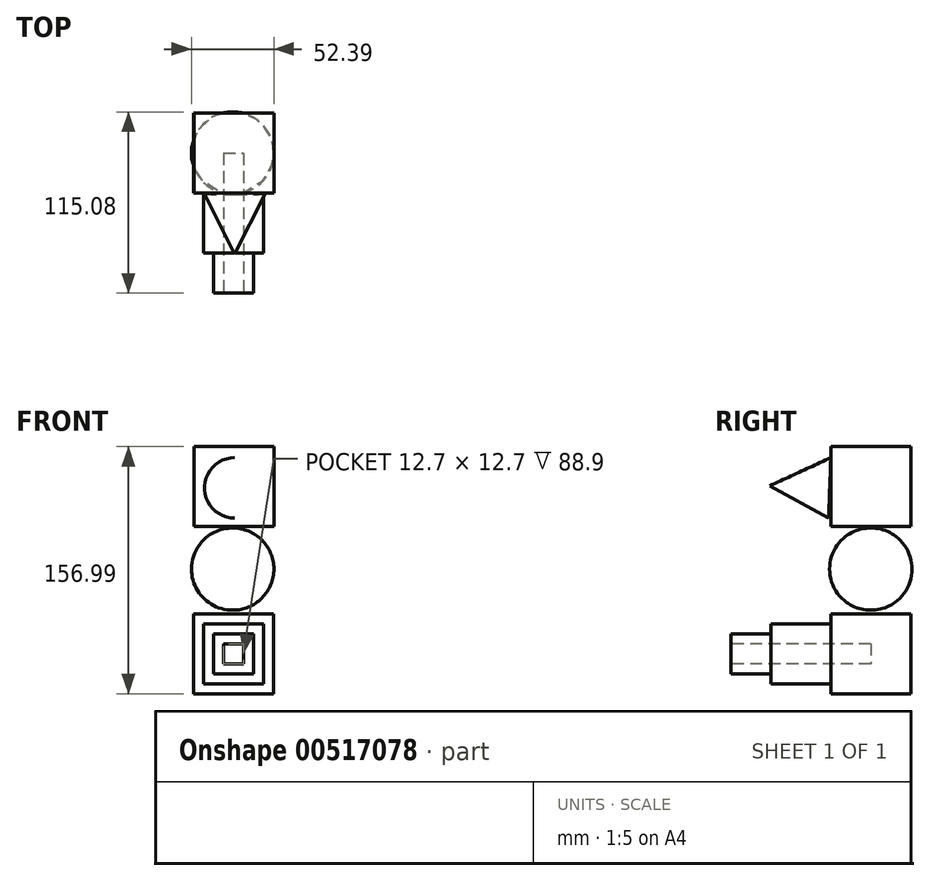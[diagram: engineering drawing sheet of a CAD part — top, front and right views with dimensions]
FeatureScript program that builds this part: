
annotation { "Feature Type Name" : "Feature", "Feature Type Description" : "" }
export const myFeature = defineFeature(function(context is Context, id is Id, definition is map)
    precondition{}
    {
        {
            var Q0;
            Q0=qCreatedBy(makeId("Front.planeOp"),FACE);
            var sketch = newSketch(context, id + "F0", { "sketchPlane" : qUnion([Q0])});
            skLineSegment(sketch, "E0", {"start": v(-36.04, 33.28) * mm, "end": v(-36.04, -51.95) * mm});
            skArc(sketch, "E1", {"start": v(-36.04, -51.95) * mm, "mid": v(4.97, -9.33) * mm, "end": v(-36.04, 33.28) * mm});
            skLineSegment(sketch, "E2.bottom", {"start": v(-68.82, 91.11) * mm, "end": v(-18.02, 91.11) * mm});
            skLineSegment(sketch, "E2.top", {"start": v(-68.82, 40.31) * mm, "end": v(-18.02, 40.31) * mm});
            skLineSegment(sketch, "E2.left", {"start": v(-68.82, 91.11) * mm, "end": v(-68.82, 40.31) * mm});
            skLineSegment(sketch, "E2.right", {"start": v(-18.02, 91.11) * mm, "end": v(-18.02, 40.31) * mm});
            skSolve(sketch);
        }
        {
            var Q0;
            Q0=makeQuery(id+"F0.imprint","IMPRINT",FACE,{"disambiguationData":[TD([[makeQuery(id+"F0.imprint","IMPRINT",EDGE,{"derivedFrom":sQuery(id+"F0.wireOp",EDGE,"E2.bottom")}),-1.0]])]});
            extrude(context, id + "F1", {"entities" : qUnion([Q0]), "depth" : 25.4 * mm, "offsetDistance" : 25.4 * mm});
        }
        {
            var Q0;
            Q0=qCreatedBy(makeId("Front.planeOp"),FACE);
            var sketch = newSketch(context, id + "F2", { "sketchPlane" : qUnion([Q0])});
            skLineSegment(sketch, "E3", {"start": v(-44.23, 39.4) * mm, "end": v(-44.23, -12.81) * mm});
            skArc(sketch, "E4", {"start": v(-44.23, -12.81) * mm, "mid": v(-18.2, 13.3) * mm, "end": v(-44.23, 39.4) * mm});
            skSolve(sketch);
        }
        {
            var Q0;
            Q0 = qSketchRegion(id + "F2", true);
            var Q1;
            Q1=sQuery(id+"F2.wireOp",EDGE,"E3");
            revolve(context, id + "F3", {"entities" : qUnion([Q0]), "axis" : qUnion([Q1]), "revolveType" : RevolveType.FULL});
        }
        {
            var Q0;
            Q0=qCreatedBy(makeId("Front.planeOp"),FACE);
            var sketch = newSketch(context, id + "F4", { "sketchPlane" : qUnion([Q0])});
            skLineSegment(sketch, "E5", {"start": v(-69.01, -15.08) * mm, "end": v(-18.21, -15.08) * mm});
            skLineSegment(sketch, "E6", {"start": v(-18.21, -15.08) * mm, "end": v(-18.21, -65.88) * mm});
            skLineSegment(sketch, "E7", {"start": v(-18.21, -65.88) * mm, "end": v(-69.01, -65.88) * mm});
            skLineSegment(sketch, "E8", {"start": v(-69.01, -65.88) * mm, "end": v(-69.01, -15.08) * mm});
            skSolve(sketch);
        }
        {
            var Q0;
            Q0=makeQuery(id+"F0.imprint","IMPRINT",FACE,{"disambiguationData":[TD([[makeQuery(id+"F0.imprint","IMPRINT",EDGE,{"derivedFrom":sQuery(id+"F0.wireOp",EDGE,"E2.bottom")}),-1.0]])]});
            extrude(context, id + "F5", {"entities" : qUnion([Q0]), "operationType" : NewBodyOperationType.ADD, "oppositeDirection" : true, "depth" : 25.4 * mm, "offsetDistance" : 25.4 * mm});
        }
        {
            var Q0;
            Q0 = qSketchRegion(id + "F4", true);
            extrude(context, id + "F6", {"entities" : qUnion([Q0]), "depth" : 25.4 * mm, "offsetDistance" : 25.4 * mm});
        }
        {
            var Q0;
            Q0=makeQuery(id+"F4.imprint","IMPRINT",FACE,{"disambiguationData":[TD([[makeQuery(id+"F4.imprint","IMPRINT",EDGE,{"derivedFrom":sQuery(id+"F4.wireOp",EDGE,"E5")}),-1.0]])]});
            extrude(context, id + "F7", {"entities" : qUnion([Q0]), "operationType" : NewBodyOperationType.ADD, "oppositeDirection" : true, "depth" : 25.4 * mm, "offsetDistance" : 25.4 * mm});
        }
        {
            var Q0;
            Q0=makeQuery(id+"F6.opExtrude","CAP_FACE",FACE,{"disambiguationData":[OSD([sQuery(id+"F4.wireOp",EDGE,"E5"),sQuery(id+"F4.wireOp",EDGE,"E6"),sQuery(id+"F4.wireOp",EDGE,"E7"),sQuery(id+"F4.wireOp",EDGE,"E8")])],"isStart":false});
            var sketch = newSketch(context, id + "F8", { "sketchPlane" : qUnion([Q0])});
            skLineSegment(sketch, "E9.bottom", {"start": v(-24.56, -21.43) * mm, "end": v(-62.66, -21.43) * mm});
            skLineSegment(sketch, "E9.top", {"start": v(-24.56, -59.53) * mm, "end": v(-62.66, -59.53) * mm});
            skLineSegment(sketch, "E9.left", {"start": v(-24.56, -21.43) * mm, "end": v(-24.56, -59.53) * mm});
            skLineSegment(sketch, "E9.right", {"start": v(-62.66, -21.43) * mm, "end": v(-62.66, -59.53) * mm});
            skPoint(sketch, "E9.middle", {"position": v(-43.61, -40.48) * mm});
            skSolve(sketch);
        }
        {
            var Q0;
            Q0=makeQuery(id+"F8.imprint","IMPRINT",FACE,{"disambiguationData":[TD([[makeQuery(id+"F8.imprint","IMPRINT",EDGE,{"derivedFrom":sQuery(id+"F8.wireOp",EDGE,"E9.bottom")}),1.0]])]});
            extrude(context, id + "F9", {"entities" : qUnion([Q0]), "operationType" : NewBodyOperationType.ADD, "depth" : 38.1 * mm, "offsetDistance" : 25.4 * mm});
        }
        {
            var Q0;
            Q0=makeQuery(id+"F9.opExtrude","CAP_FACE",FACE,{"disambiguationData":[OSD([sQuery(id+"F8.wireOp",EDGE,"E9.bottom"),sQuery(id+"F8.wireOp",EDGE,"E9.top"),sQuery(id+"F8.wireOp",EDGE,"E9.left"),sQuery(id+"F8.wireOp",EDGE,"E9.right")])],"isStart":false});
            var sketch = newSketch(context, id + "F10", { "sketchPlane" : qUnion([Q0])});
            skLineSegment(sketch, "E10.bottom", {"start": v(-30.91, -27.78) * mm, "end": v(-56.31, -27.78) * mm});
            skLineSegment(sketch, "E10.top", {"start": v(-30.91, -53.18) * mm, "end": v(-56.31, -53.18) * mm});
            skLineSegment(sketch, "E10.left", {"start": v(-30.91, -27.78) * mm, "end": v(-30.91, -53.18) * mm});
            skLineSegment(sketch, "E10.right", {"start": v(-56.31, -27.78) * mm, "end": v(-56.31, -53.18) * mm});
            skPoint(sketch, "E10.middle", {"position": v(-43.61, -40.48) * mm});
            skSolve(sketch);
        }
        {
            var Q0;
            Q0=makeQuery(id+"F10.imprint","IMPRINT",FACE,{"disambiguationData":[TD([[makeQuery(id+"F10.imprint","IMPRINT",EDGE,{"derivedFrom":sQuery(id+"F10.wireOp",EDGE,"E10.bottom")}),1.0]])]});
            extrude(context, id + "F11", {"entities" : qUnion([Q0]), "operationType" : NewBodyOperationType.ADD, "depth" : 25.4 * mm, "offsetDistance" : 25.4 * mm});
        }
        {
            var Q0;
            Q0=makeQuery(id+"F11.opExtrude","CAP_FACE",FACE,{"disambiguationData":[OSD([sQuery(id+"F10.wireOp",EDGE,"E10.bottom"),sQuery(id+"F10.wireOp",EDGE,"E10.top"),sQuery(id+"F10.wireOp",EDGE,"E10.left"),sQuery(id+"F10.wireOp",EDGE,"E10.right")])],"isStart":false});
            var sketch = newSketch(context, id + "F12", { "sketchPlane" : qUnion([Q0])});
            skLineSegment(sketch, "E11.bottom", {"start": v(-49.96, -34.13) * mm, "end": v(-37.26, -34.13) * mm});
            skLineSegment(sketch, "E11.top", {"start": v(-49.96, -46.83) * mm, "end": v(-37.26, -46.83) * mm});
            skLineSegment(sketch, "E11.left", {"start": v(-49.96, -34.13) * mm, "end": v(-49.96, -46.83) * mm});
            skLineSegment(sketch, "E11.right", {"start": v(-37.26, -34.13) * mm, "end": v(-37.26, -46.83) * mm});
            skSolve(sketch);
        }
        {
            var Q0;
            Q0=makeQuery(id+"F12.imprint","IMPRINT",FACE,{"disambiguationData":[TD([[makeQuery(id+"F12.imprint","IMPRINT",EDGE,{"derivedFrom":sQuery(id+"F12.wireOp",EDGE,"E11.bottom")}),-1.0]])]});
            extrude(context, id + "F13", {"entities" : qUnion([Q0]), "operationType" : NewBodyOperationType.REMOVE, "oppositeDirection" : true, "depth" : 88.9 * mm, "offsetDistance" : 25.4 * mm});
        }
        {
            var Q0;
            Q0=qCreatedBy(makeId("Right.planeOp"),FACE);
            var sketch = newSketch(context, id + "F14", { "sketchPlane" : qUnion([Q0])});
            skLineSegment(sketch, "E12", {"start": v(-25.4, 85.04) * mm, "end": v(-25.4, 65.85) * mm});
            skLineSegment(sketch, "E13", {"start": v(-25.4, 65.85) * mm, "end": v(-64.15, 67.22) * mm});
            skLineSegment(sketch, "E14", {"start": v(-64.15, 67.22) * mm, "end": v(-25.4, 85.04) * mm});
            skSolve(sketch);
        }
        {
            var Q0;
            Q0=makeQuery(id+"F14.imprint","IMPRINT",FACE,{"disambiguationData":[TD([[makeQuery(id+"F14.imprint","IMPRINT",EDGE,{"derivedFrom":sQuery(id+"F14.wireOp",EDGE,"E12")}),-1.0]])]});
            var Q1;
            Q1=sQuery(id+"F14.wireOp",EDGE,"E13");
            revolve(context, id + "F15", {"entities" : qUnion([Q0]), "axis" : qUnion([Q1]), "revolveType" : RevolveType.FULL});
        }
        {
            var Q0;
            Q0=makeQuery(id+"F15.opRevolve","SWEPT_BODY",BODY,{"disambiguationData":[OSD([sQuery(id+"F14.wireOp",EDGE,"E12"),sQuery(id+"F14.wireOp",EDGE,"E13"),sQuery(id+"F14.wireOp",EDGE,"E14")])]});
            transform(context, id + "F16", {"entities" : qUnion([Q0]), "transformType" : TransformType.TRANSLATION_3D, "dx" : -42.93 * mm, "dy" : 0 * mm, "dz" : -1.02 * mm, "makeCopy" : false});
        }
    });
